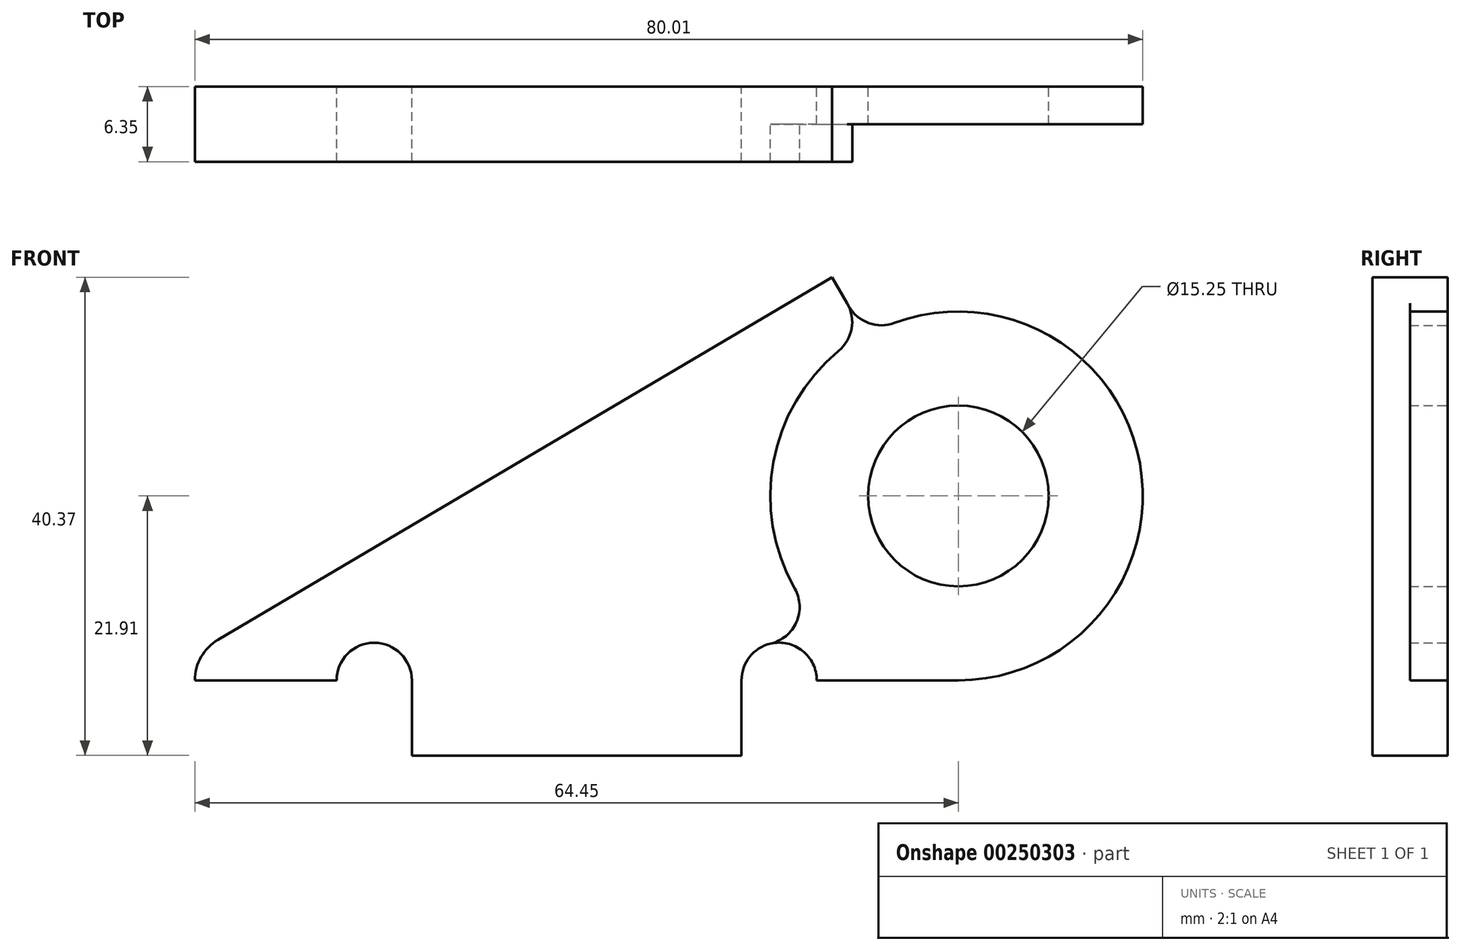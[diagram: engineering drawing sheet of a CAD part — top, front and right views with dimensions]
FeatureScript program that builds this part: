
annotation { "Feature Type Name" : "Feature", "Feature Type Description" : "" }
export const myFeature = defineFeature(function(context is Context, id is Id, definition is map)
    precondition{}
    {
        {
            var Q0;
            Q0=qCreatedBy(makeId("Front.planeOp"),FACE);
            var sketch = newSketch(context, id + "F0", { "sketchPlane" : qUnion([Q0])});
            skLineSegment(sketch, "E0", {"start": v(-46.14, -21.91) * mm, "end": v(-18.3, -21.91) * mm});
            skLineSegment(sketch, "E1", {"start": v(-46.14, -15.56) * mm, "end": v(-46.14, -21.91) * mm});
            skArc(sketch, "E2", {"start": v(-46.14, -15.56) * mm, "mid": v(-49.32, -12.39) * mm, "end": v(-52.5, -15.56) * mm});
            skLineSegment(sketch, "E3", {"start": v(-64.45, -15.56) * mm, "end": v(-52.5, -15.56) * mm});
            skArc(sketch, "E4", {"start": v(-62.5, -12.14) * mm, "mid": v(-63.93, -13.6) * mm, "end": v(-64.45, -15.56) * mm});
            skLineSegment(sketch, "E5", {"start": v(-10.66, 18.46) * mm, "end": v(-62.5, -12.14) * mm});
            skLineSegment(sketch, "E6", {"start": v(-9.23, 16) * mm, "end": v(-10.66, 18.46) * mm});
            skArc(sketch, "E7", {"start": v(-9.23, 16) * mm, "mid": v(-7.56, 14.6) * mm, "end": v(-5.39, 14.6) * mm});
            skArc(sketch, "E8", {"start": v(0, -15.56) * mm, "mid": v(15.32, 2.74) * mm, "end": v(-5.39, 14.6) * mm});
            skLineSegment(sketch, "E9", {"start": v(-11.96, -15.56) * mm, "end": v(0, -15.56) * mm});
            skArc(sketch, "E10", {"start": v(-11.96, -15.56) * mm, "mid": v(-15.13, -12.39) * mm, "end": v(-18.3, -15.56) * mm});
            skLineSegment(sketch, "E11", {"start": v(-18.3, -21.91) * mm, "end": v(-18.3, -15.56) * mm});
            skArc(sketch, "E12", {"start": v(-15.86, -12.47) * mm, "mid": v(-13.67, -10.66) * mm, "end": v(-13.82, -7.82) * mm});
            skArc(sketch, "E13", {"start": v(-10.12, 12.23) * mm, "mid": v(-15.61, 2.88) * mm, "end": v(-13.82, -7.82) * mm});
            skArc(sketch, "E14", {"start": v(-10.12, 12.23) * mm, "mid": v(-9.02, 14.12) * mm, "end": v(-9.4, 16.27) * mm});
            skCircle(sketch, "E15", {"center": v(0, 0) * mm, "radius": 7.63 * mm});
            skSolve(sketch);
        }
        {
            var Q0;
            {var subQ1=sQuery(id+"F0.wireOp",EDGE,"E7");Q0=makeQuery(id+"F0.imprint","IMPRINT",FACE,{"disambiguationData":[TD([[makeQuery(id+"F0.imprint","IMPRINT",EDGE,{"derivedFrom":subQ1}),-1.0]])]});}
            extrude(context, id + "F1", {"entities" : qUnion([Q0]), "depth" : 3.17 * mm});
        }
        {
            var Q0;
            Q0=makeQuery(id+"F0.imprint","IMPRINT",FACE,{"disambiguationData":[TD([[makeQuery(id+"F0.imprint","IMPRINT",EDGE,{"derivedFrom":sQuery(id+"F0.wireOp",EDGE,"E0")}),1.0]])]});
            extrude(context, id + "F2", {"entities" : qUnion([Q0]), "operationType" : NewBodyOperationType.ADD, "depth" : 6.35 * mm});
        }
    });
